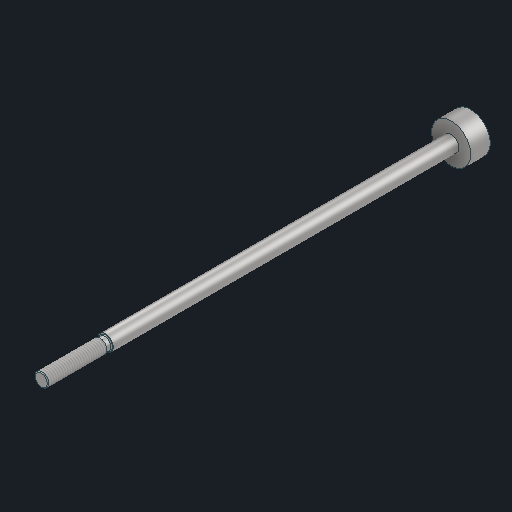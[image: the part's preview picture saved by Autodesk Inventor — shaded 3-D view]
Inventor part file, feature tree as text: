
AUTODESK INVENTOR PART (.ipt)
format: ipt  version: 2024 (Build 280153000, 153)  size: 125,952 bytes
history: native  units: in
note: dims shown in document units (in); Inventor stores cm internally (conversion verified against a paired STEP export)
features: thread x2
ambient origin geometry x8: Origin, YZ Plane, XZ Plane, XY Plane, X Axis, Y Axis, Z Axis, Center Point
bodies: Solid1 (feature_tree)
feature tree (2):
  thread  "Thread1"  [1 undecoded]
  thread  "Threads"  [1 undecoded]
note: 2 required parameter values undecoded (feature->parameter linkage not recoverable at this tier; creation-order binding heuristic only, values carry confidence <= 0.55)
